# Revit family: FLOWAIR ELiS C-E-100-bílá
name_source: partatom
category: Electrical Fixtures
revit_build: Autodesk Revit LT 2018 (Build: 20180329_1100(x64)
units: mm (PartAtom-declared; Revit-internal decimal feet)

## family parameters
Cut with Voids When Loaded = No
Host = Face
Maintain Annotation Orientation = No
Part Type = Normal
Room Calculation Point = No
Round Connector Dimension = Use Diameter
Shared = No

## types (6) — shared parameters
Default Elevation = 2200 mm
Description = Dveřní clona
Fan = Single phase motor with diagonal rotor
IP = 21
Length = 1000 mm  [stored 3.28084 ft]
Load classification = Other
Main Material = FLOWAIR-Steel-White
Manufacturer = Hydronic Systems Prague s.r.o.
Model = ELiS C-E-100
Power ratio = 1
Product code = 14290; bílá, délka 100cm, elektrická
Second Material = FLOWAIR-PerforatedSteel-White
Type Comments = vnitřní instalace, neprašné prostředí; IP21; max dosah 3m na 3 rychlost
URL = www.hydronic.cz
Weight of unit = 14.50 kg

## per-type parameters (varying)
| type | Apparent power | Heating capacity | Number of phases | Power supply | Rated current |
| ELiS C-E-100, 3x400V, 1 rychlost | 6072 VA | 6.1 kW | 3 | 400 V | 9 A |
| ELiS C-E-100, 3x400V, 2 rychlost | 6279 VA | 6.4 kW | 3 | 400 V | 9 A |
| ELiS C-E-100, 3x400V, 3 rychlost | 6486 VA | 6.5 kW | 3 | 400 V | 9 A |
| ELiS C-E-100, 1x230V, 1 rychlost | 6072 VA | 6.1 kW | 1 | 230 V | 26 A |
| ELiS C-E-100, 1x230V, 2 rychlost | 6279 VA | 6.4 kW | 1 | 230 V | 27 A |
| ELiS C-E-100, 1x230V, 3 rychlost | 6486 VA | 6.5 kW | 1 | 230 V | 28 A |

note: [stored X ft] marks values corroborated as IEEE doubles in the binary element streams (Revit-internal decimal feet)
